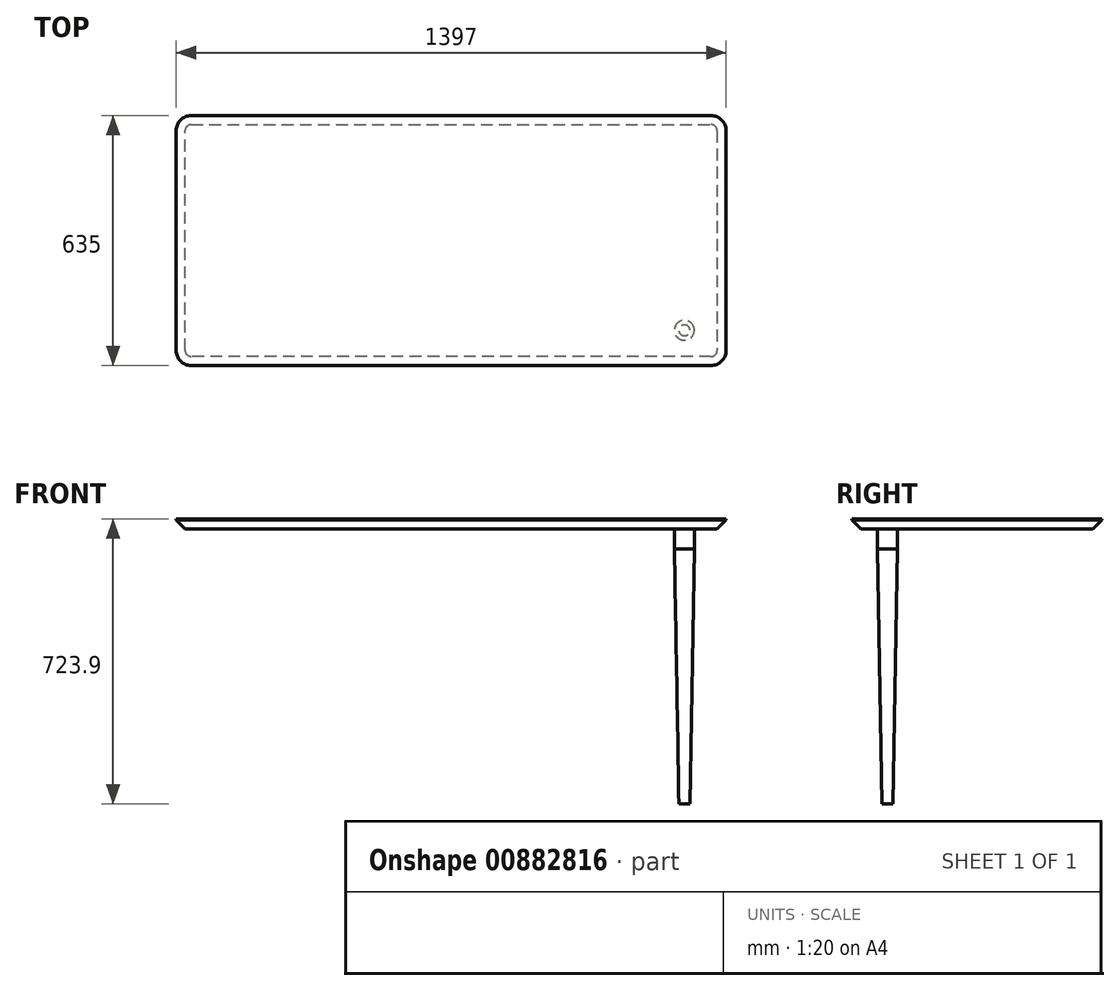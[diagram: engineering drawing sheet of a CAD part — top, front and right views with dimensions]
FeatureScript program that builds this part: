
annotation { "Feature Type Name" : "Feature", "Feature Type Description" : "" }
export const myFeature = defineFeature(function(context is Context, id is Id, definition is map)
    precondition{}
    {
        {
            var Q0;
            Q0=qCreatedBy(makeId("Top.planeOp"),FACE);
            var sketch = newSketch(context, id + "F0", { "sketchPlane" : qUnion([Q0])});
            skLineSegment(sketch, "E0.bottom", {"start": v(698.5, 317.5) * mm, "end": v(-698.5, 317.5) * mm});
            skLineSegment(sketch, "E0.top", {"start": v(698.5, -317.5) * mm, "end": v(-698.5, -317.5) * mm});
            skLineSegment(sketch, "E0.left", {"start": v(698.5, 317.5) * mm, "end": v(698.5, -317.5) * mm});
            skLineSegment(sketch, "E0.right", {"start": v(-698.5, 317.5) * mm, "end": v(-698.5, -317.5) * mm});
            skPoint(sketch, "E0.middle", {"position": v(0, 0) * mm});
            skSolve(sketch);
        }
        {
            var Q0;
            Q0 = qSketchRegion(id + "F0", true);
            extrude(context, id + "F1", {"entities" : qUnion([Q0]), "depth" : 25.4 * mm, "offsetDistance" : 25.4 * mm});
        }
        {
            var Q0;
            Q0=makeQuery(id+"F1.opExtrude","SWEPT_EDGE",EDGE,{"disambiguationData":[OSD([sQuery(id+"F0.wireOp",EDGE,"E0.top"),sQuery(id+"F0.wireOp",EDGE,"E0.right")])]});
            var Q1;
            Q1=makeQuery(id+"F1.opExtrude","SWEPT_EDGE",EDGE,{"disambiguationData":[OSD([sQuery(id+"F0.wireOp",EDGE,"E0.top"),sQuery(id+"F0.wireOp",EDGE,"E0.left")])]});
            var Q2;
            Q2=makeQuery(id+"F1.opExtrude","SWEPT_EDGE",EDGE,{"disambiguationData":[OSD([sQuery(id+"F0.wireOp",EDGE,"E0.bottom"),sQuery(id+"F0.wireOp",EDGE,"E0.left")])]});
            var Q3;
            Q3=makeQuery(id+"F1.opExtrude","SWEPT_EDGE",EDGE,{"disambiguationData":[OSD([sQuery(id+"F0.wireOp",EDGE,"E0.bottom"),sQuery(id+"F0.wireOp",EDGE,"E0.right")])]});
            fillet(context, id + "F2", {"entities" : qUnion([Q0, Q1, Q2, Q3]), "tangentPropagation" : true, "radius" : 38.1 * mm, "defaultsChanged" : false, "vertexSettings" : [], "allowEdgeOverflow" : false});
        }
        {
            var Q0;
            Q0=makeQuery(id+"F1.opExtrude","CAP_EDGE",EDGE,{"disambiguationData":[OSD([sQuery(id+"F0.wireOp",EDGE,"E0.bottom")])],"isStart":true});
            chamfer(context, id + "F3", {"entities" : qUnion([Q0]), "width" : 22.86 * mm, "tangentPropagation" : true});
        }
        {
            var Q0;
            Q0=makeQuery(id+"F1.opExtrude","CAP_FACE",FACE,{"disambiguationData":[OSD([sQuery(id+"F0.wireOp",EDGE,"E0.bottom"),sQuery(id+"F0.wireOp",EDGE,"E0.top"),sQuery(id+"F0.wireOp",EDGE,"E0.left"),sQuery(id+"F0.wireOp",EDGE,"E0.right")])],"isStart":true});
            var sketch = newSketch(context, id + "F4", { "sketchPlane" : qUnion([Q0])});
            skCircle(sketch, "E1", {"center": v(592.51, 227.9) * mm, "radius": 25.4 * mm});
            skSolve(sketch);
        }
        {
            var Q0;
            Q0 = qSketchRegion(id + "F4", true);
            extrude(context, id + "F5", {"entities" : qUnion([Q0]), "flatOperationType" : FlatOperationType.REMOVE, "depth" : 50.8 * mm, "offsetDistance" : 25.4 * mm, "domain" : OperationDomain.MODEL});
        }
        {
            var Q0;
            Q0=makeQuery(id+"F5.opExtrude","CAP_FACE",FACE,{"disambiguationData":[OSD([sQuery(id+"F4.wireOp",EDGE,"E1")])],"isStart":false});
            var sketch = newSketch(context, id + "F6", { "sketchPlane" : qUnion([Q0])});
            skCircle(sketch, "E2", {"center": v(592.51, 227.9) * mm, "radius": 25.23 * mm});
            skSolve(sketch);
        }
        {
            var Q0;
            Q0 = qSketchRegion(id + "F6", true);
            extrude(context, id + "F7", {"entities" : qUnion([Q0]), "operationType" : NewBodyOperationType.ADD, "depth" : 647.7 * mm, "offsetDistance" : 25.4 * mm, "hasDraft" : true, "draftAngle" : 1 * degree, "draftPullDirection" : true});
        }
        {
            var Q0;
            Q0=makeQuery(id+"F1.opExtrude","SWEPT_BODY",BODY,{"disambiguationData":[OSD([sQuery(id+"F0.wireOp",EDGE,"E0.bottom"),sQuery(id+"F0.wireOp",EDGE,"E0.top"),sQuery(id+"F0.wireOp",EDGE,"E0.left"),sQuery(id+"F0.wireOp",EDGE,"E0.right")])]});
            var Q1;
            Q1=qCreatedBy(makeId("Front.planeOp"),FACE);
            mirror(context, id + "F8", {"operationType" : NewBodyOperationType.ADD, "entities" : qUnion([Q0]), "mirrorPlane" : qUnion([Q1])});
        }
    });
